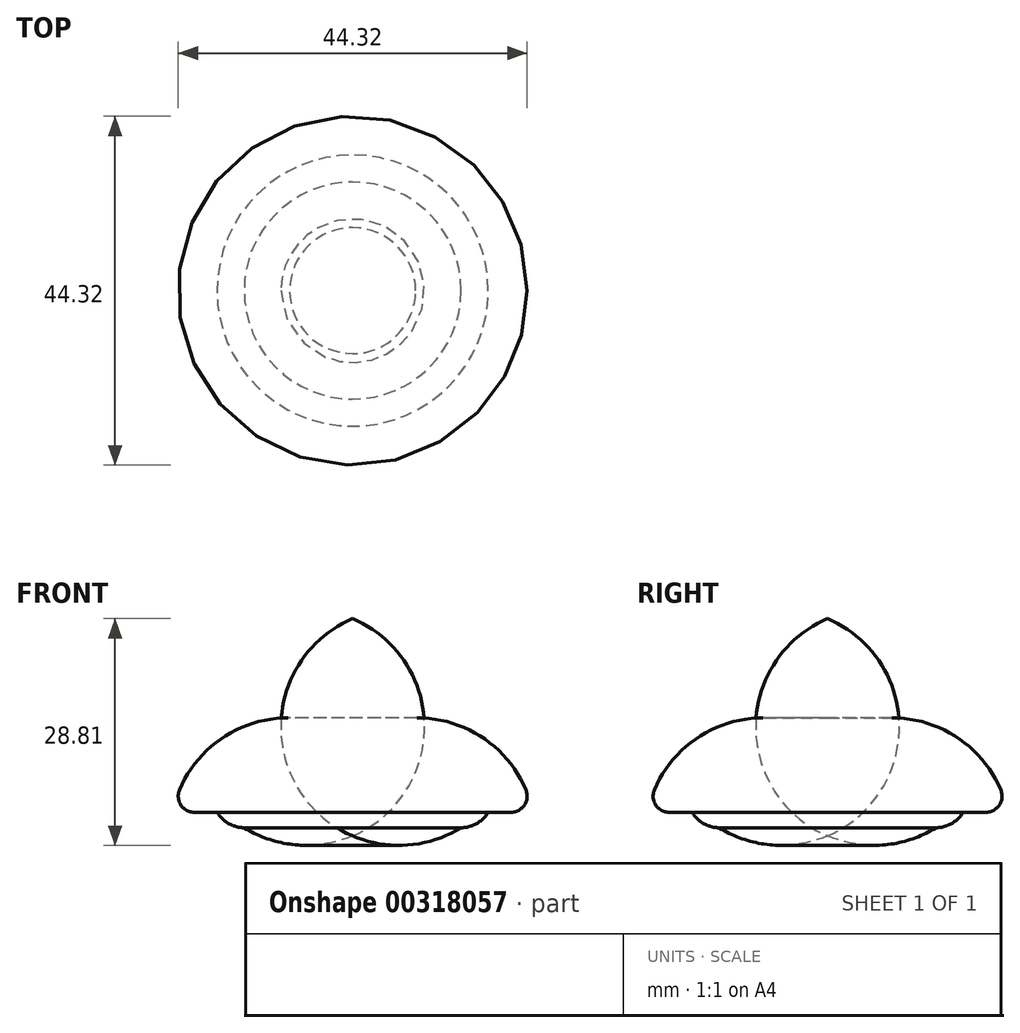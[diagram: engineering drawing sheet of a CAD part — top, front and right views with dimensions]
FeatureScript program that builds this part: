
annotation { "Feature Type Name" : "Feature", "Feature Type Description" : "" }
export const myFeature = defineFeature(function(context is Context, id is Id, definition is map)
    precondition{}
    {
        {
            var Q0;
            Q0=qCreatedBy(makeId("Front.planeOp"),FACE);
            var sketch = newSketch(context, id + "F0", { "sketchPlane" : qUnion([Q0])});
            skArc(sketch, "E0", {"start": v(22, -9.16) * mm, "mid": v(16.4, -2.45) * mm, "end": v(8, 0) * mm});
            skArc(sketch, "E1", {"start": v(13.78, -13.96) * mm, "mid": v(15.76, -13.43) * mm, "end": v(17.22, -12) * mm});
            skLineSegment(sketch, "E2", {"start": v(17.22, -12) * mm, "end": v(20.12, -12) * mm});
            skArc(sketch, "E3", {"start": v(20.12, -12) * mm, "mid": v(21.82, -11.09) * mm, "end": v(22, -9.16) * mm});
            skLineSegment(sketch, "E4", {"start": v(8, 0) * mm, "end": v(0, 0) * mm});
            skLineSegment(sketch, "E5", {"start": v(0, 0) * mm, "end": v(0, -15) * mm});
            skArc(sketch, "E6", {"start": v(0, -15) * mm, "mid": v(7.02, -16.16) * mm, "end": v(13.78, -13.96) * mm});
            skSolve(sketch);
        }
        {
            var Q0;
            Q0 = qSketchRegion(id + "F0", true);
            var Q1;
            Q1=sQuery(id+"F0.wireOp",EDGE,"E5");
            revolve(context, id + "F1", {"entities" : qUnion([Q0]), "axis" : qUnion([Q1]), "revolveType" : RevolveType.FULL});
        }
    });
